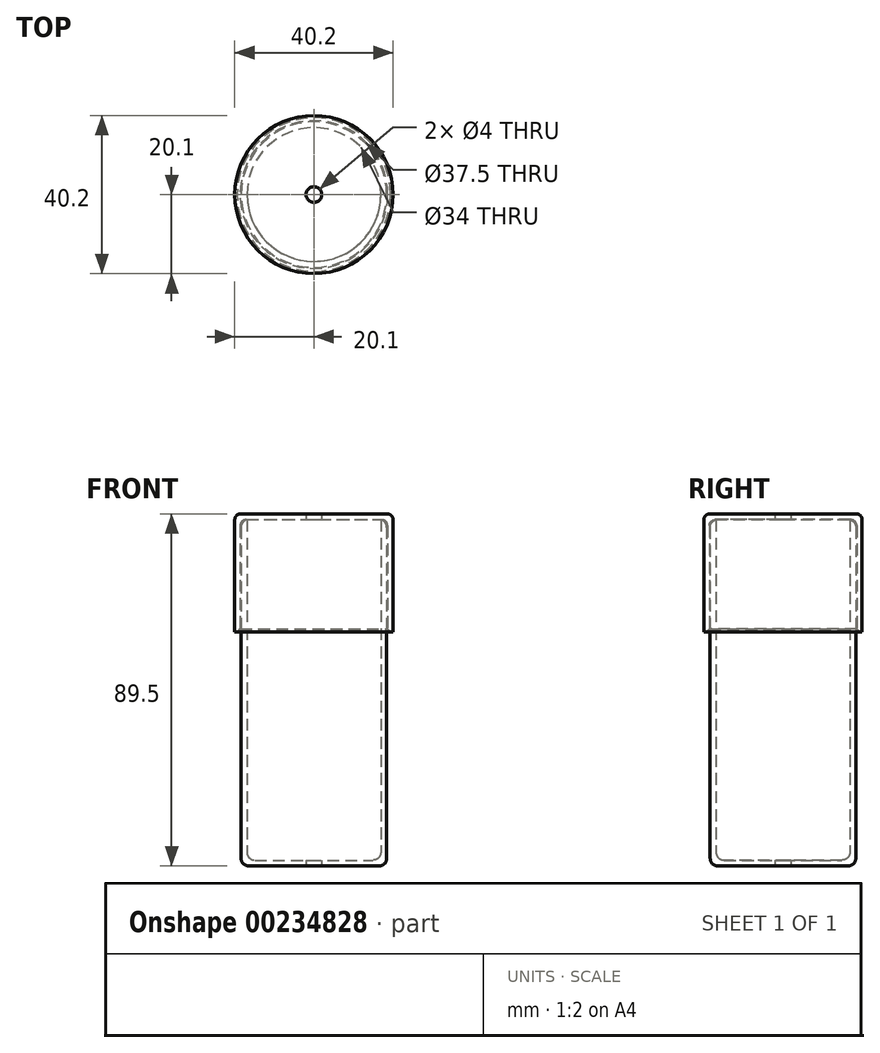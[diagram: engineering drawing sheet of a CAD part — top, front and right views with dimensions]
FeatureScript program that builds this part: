
annotation { "Feature Type Name" : "Feature", "Feature Type Description" : "" }
export const myFeature = defineFeature(function(context is Context, id is Id, definition is map)
    precondition{}
    {
        {
            var Q0;
            Q0=qCreatedBy(makeId("Front.planeOp"),FACE);
            var sketch = newSketch(context, id + "F0", { "sketchPlane" : qUnion([Q0])});
            skLineSegment(sketch, "E0", {"start": v(-2, 1.5) * mm, "end": v(-17, 1.5) * mm});
            skLineSegment(sketch, "E1", {"start": v(-17, 1.5) * mm, "end": v(-17, 88) * mm});
            skLineSegment(sketch, "E2", {"start": v(-17, 88) * mm, "end": v(-18.5, 88) * mm});
            skLineSegment(sketch, "E3", {"start": v(-18.5, 88) * mm, "end": v(-18.5, 0) * mm});
            skLineSegment(sketch, "E4", {"start": v(-18.5, 0) * mm, "end": v(-2, 0) * mm});
            skLineSegment(sketch, "E5", {"start": v(-2, 0) * mm, "end": v(-2, 1.5) * mm});
            skLineSegment(sketch, "E6", {"start": v(0, 0) * mm, "end": v(0, 77.46) * mm, "construction": true});
            skSolve(sketch);
        }
        {
            var Q0;
            Q0 = qSketchRegion(id + "F0", true);
            var Q1;
            Q1=sQuery(id+"F0.wireOp",EDGE,"E6");
            revolve(context, id + "F1", {"entities" : qUnion([Q0]), "axis" : qUnion([Q1]), "revolveType" : RevolveType.FULL});
        }
        {
            var Q0;
            Q0=makeQuery(id+"F1.opRevolve","SWEPT_EDGE",EDGE,{"disambiguationData":[OSD([sQuery(id+"F0.wireOp",EDGE,"E0"),sQuery(id+"F0.wireOp",EDGE,"E1")])]});
            var Q1;
            Q1=makeQuery(id+"F1.opRevolve","SWEPT_EDGE",EDGE,{"disambiguationData":[OSD([sQuery(id+"F0.wireOp",EDGE,"E3"),sQuery(id+"F0.wireOp",EDGE,"E4")])]});
            var Q2;
            Q2=makeQuery(id+"F1.opRevolve","SWEPT_EDGE",EDGE,{"disambiguationData":[OSD([sQuery(id+"F0.wireOp",EDGE,"E2"),sQuery(id+"F0.wireOp",EDGE,"E3")])]});
            fillet(context, id + "F2", {"entities" : qUnion([Q0, Q1, Q2]), "radius" : 2 * mm, "tangentPropagation" : true, "allowEdgeOverflow" : false});
        }
        {
            var Q0;
            Q0=qCreatedBy(makeId("Front.planeOp"),FACE);
            var sketch = newSketch(context, id + "F3", { "sketchPlane" : qUnion([Q0])});
            skLineSegment(sketch, "E7", {"start": v(-20.1, 59.5) * mm, "end": v(-19.5, 59.5) * mm});
            skLineSegment(sketch, "E8", {"start": v(-18.75, 60.25) * mm, "end": v(-18.75, 86.5) * mm});
            skLineSegment(sketch, "E9", {"start": v(-17.25, 88) * mm, "end": v(-2, 88) * mm});
            skLineSegment(sketch, "E10", {"start": v(-2, 88) * mm, "end": v(-2, 89.5) * mm});
            skLineSegment(sketch, "E11", {"start": v(-2, 89.5) * mm, "end": v(-18.6, 89.5) * mm});
            skLineSegment(sketch, "E12", {"start": v(-20.1, 88) * mm, "end": v(-20.1, 59.5) * mm});
            skLineSegment(sketch, "E13", {"start": v(0, 0) * mm, "end": v(0, 48.8) * mm, "construction": true});
            skPoint(sketch, "E14.visualSharp", {"position": v(-20.1, 89.5) * mm});
            skArc(sketch, "E14.filletArc", {"start": v(-18.6, 89.5) * mm, "mid": v(-19.66, 89.06) * mm, "end": v(-20.1, 88) * mm});
            skPoint(sketch, "E15.visualSharp", {"position": v(-18.75, 88) * mm});
            skArc(sketch, "E15.filletArc", {"start": v(-17.25, 88) * mm, "mid": v(-18.31, 87.56) * mm, "end": v(-18.75, 86.5) * mm});
            skLineSegment(sketch, "E16", {"start": v(-18.75, 60.25) * mm, "end": v(-19.5, 59.5) * mm});
            skSolve(sketch);
        }
        {
            var Q0;
            Q0 = qSketchRegion(id + "F3", true);
            var Q1;
            Q1=sQuery(id+"F3.wireOp",EDGE,"E13");
            revolve(context, id + "F4", {"entities" : qUnion([Q0]), "axis" : qUnion([Q1]), "revolveType" : RevolveType.FULL});
        }
    });
